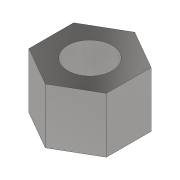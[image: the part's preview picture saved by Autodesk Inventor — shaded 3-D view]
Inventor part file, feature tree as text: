
AUTODESK INVENTOR PART (.ipt)
format: ipt  version: 2022 (Build 260153000, 153)  size: 91,648 bytes
history: native  units: mm
features: extrude x1, sketch x1
ambient origin geometry x8: Origin, YZ Plane, XZ Plane, XY Plane, X Axis, Y Axis, Z Axis, Center Point
bodies: Solid1 (feature_tree)
feature tree (2):
  extrude  "Extrusion1"  Depth=5.0mm
  sketch  "Sketch1"  dims[d0=7.0mm d1=4.0mm d2=5.0mm d3=0.0mm]
